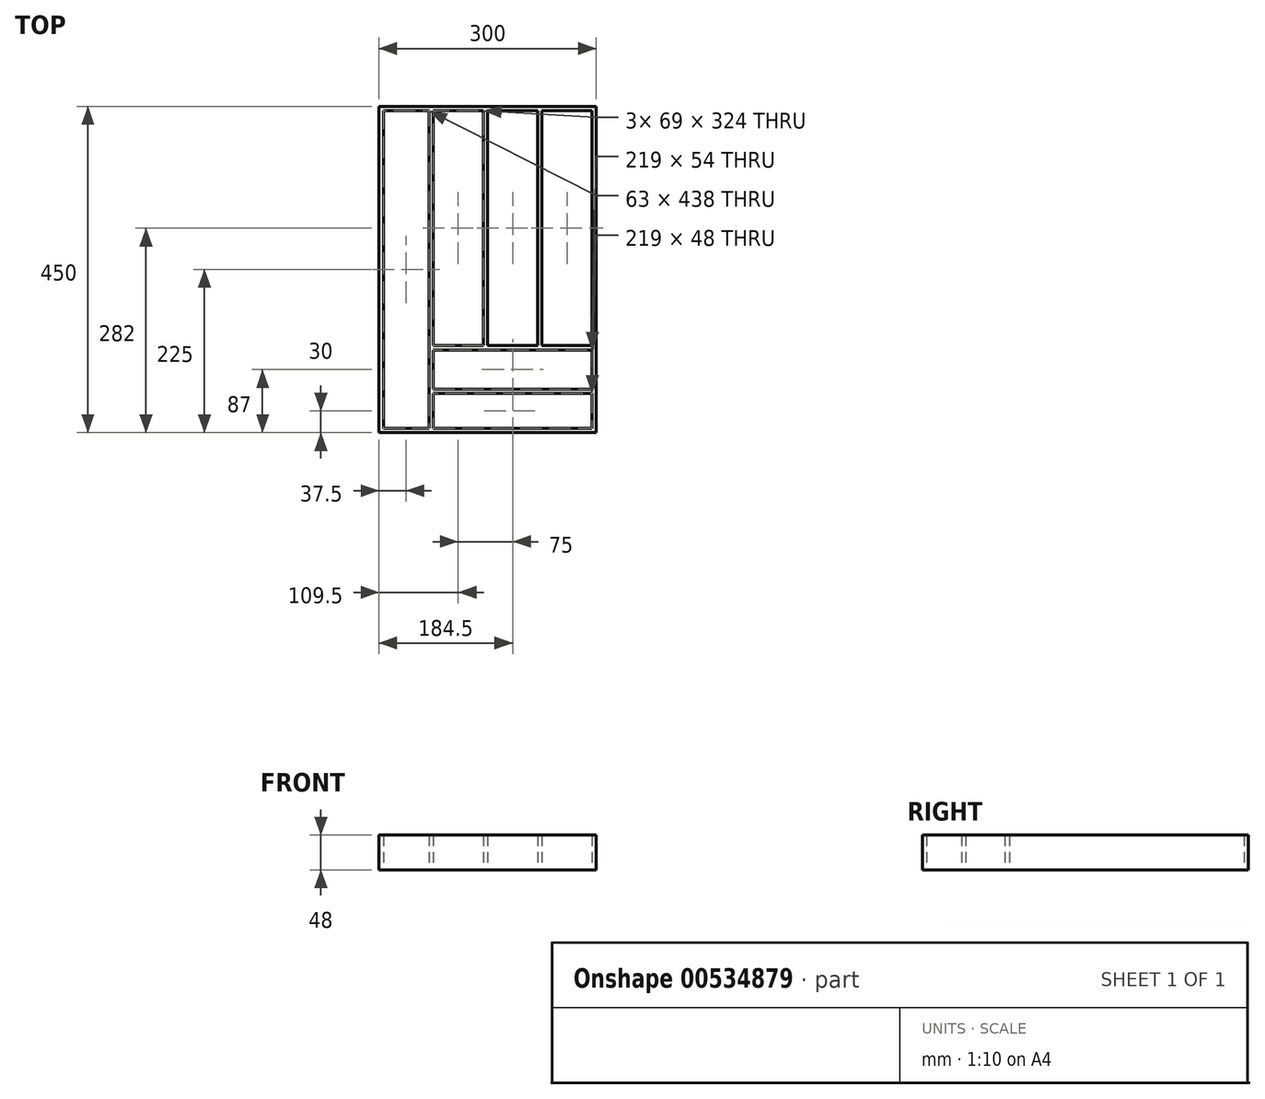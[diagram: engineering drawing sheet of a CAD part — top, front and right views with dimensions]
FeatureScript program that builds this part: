
annotation { "Feature Type Name" : "Feature", "Feature Type Description" : "" }
export const myFeature = defineFeature(function(context is Context, id is Id, definition is map)
    precondition{}
    {
        {
            var Q0;
            Q0=qCreatedBy(makeId("Top.planeOp"),FACE);
            var sketch = newSketch(context, id + "F0", { "sketchPlane" : qUnion([Q0])});
            skLineSegment(sketch, "E0.bottom", {"start": v(150, 225) * mm, "end": v(-150, 225) * mm});
            skLineSegment(sketch, "E0.top", {"start": v(150, -225) * mm, "end": v(-150, -225) * mm});
            skLineSegment(sketch, "E0.left", {"start": v(150, 225) * mm, "end": v(150, -225) * mm});
            skLineSegment(sketch, "E0.right", {"start": v(-150, 225) * mm, "end": v(-150, -225) * mm});
            skPoint(sketch, "E0.middle", {"position": v(0, 0) * mm});
            skLineSegment(sketch, "E1", {"start": v(-75, 219) * mm, "end": v(-75, -105) * mm});
            skLineSegment(sketch, "E2", {"start": v(-75, -165) * mm, "end": v(144, -165) * mm});
            skLineSegment(sketch, "E3", {"start": v(-75, -105) * mm, "end": v(-6, -105) * mm});
            skLineSegment(sketch, "E4", {"start": v(0, 219) * mm, "end": v(0, -105) * mm});
            skLineSegment(sketch, "E5", {"start": v(75, 219) * mm, "end": v(75, -105) * mm});
            skLineSegment(sketch, "E6.0", {"start": v(-144, 219) * mm, "end": v(-144, -219) * mm});
            skLineSegment(sketch, "E6.1", {"start": v(144, 219) * mm, "end": v(75, 219) * mm});
            skLineSegment(sketch, "E6.2", {"start": v(144, 219) * mm, "end": v(144, -105) * mm});
            skLineSegment(sketch, "E6.3", {"start": v(144, -219) * mm, "end": v(-75, -219) * mm});
            skLineSegment(sketch, "E7.0", {"start": v(-81, 219) * mm, "end": v(-81, -219) * mm});
            skLineSegment(sketch, "E8.0", {"start": v(-6, 219) * mm, "end": v(-6, -105) * mm});
            skLineSegment(sketch, "E9.0", {"start": v(69, 219) * mm, "end": v(69, -105) * mm});
            skLineSegment(sketch, "E10.0", {"start": v(-75, -111) * mm, "end": v(144, -111) * mm});
            skLineSegment(sketch, "E11.0", {"start": v(-75, -171) * mm, "end": v(144, -171) * mm});
            skLineSegment(sketch, "E12.trimOffspring", {"start": v(69, 219) * mm, "end": v(0, 219) * mm});
            skLineSegment(sketch, "E13.trimOffspring", {"start": v(-6, 219) * mm, "end": v(-75, 219) * mm});
            skLineSegment(sketch, "E14.trimOffspring", {"start": v(-81, 219) * mm, "end": v(-144, 219) * mm});
            skLineSegment(sketch, "E15.trimOffspring", {"start": v(75, -105) * mm, "end": v(144, -105) * mm});
            skLineSegment(sketch, "E16.trimOffspring", {"start": v(0, -105) * mm, "end": v(69, -105) * mm});
            skLineSegment(sketch, "E17.trimOffspring", {"start": v(-75, -111) * mm, "end": v(-75, -165) * mm});
            skLineSegment(sketch, "E18.trimOffspring", {"start": v(144, -111) * mm, "end": v(144, -165) * mm});
            skLineSegment(sketch, "E19.trimOffspring", {"start": v(144, -171) * mm, "end": v(144, -219) * mm});
            skLineSegment(sketch, "E20.trimOffspring", {"start": v(-75, -171) * mm, "end": v(-75, -219) * mm});
            skLineSegment(sketch, "E21.trimOffspring", {"start": v(-81, -219) * mm, "end": v(-144, -219) * mm});
            skSolve(sketch);
        }
        {
            var Q0;
            Q0=makeQuery(id+"F0.imprint","IMPRINT",FACE,{"disambiguationData":[TD([[makeQuery(id+"F0.imprint","IMPRINT",EDGE,{"derivedFrom":sQuery(id+"F0.wireOp",EDGE,"E0.bottom")}),1.0]])]});
            extrude(context, id + "F1", {"entities" : qUnion([Q0]), "depth" : 48 * mm, "offsetDistance" : 25 * mm});
        }
    });
